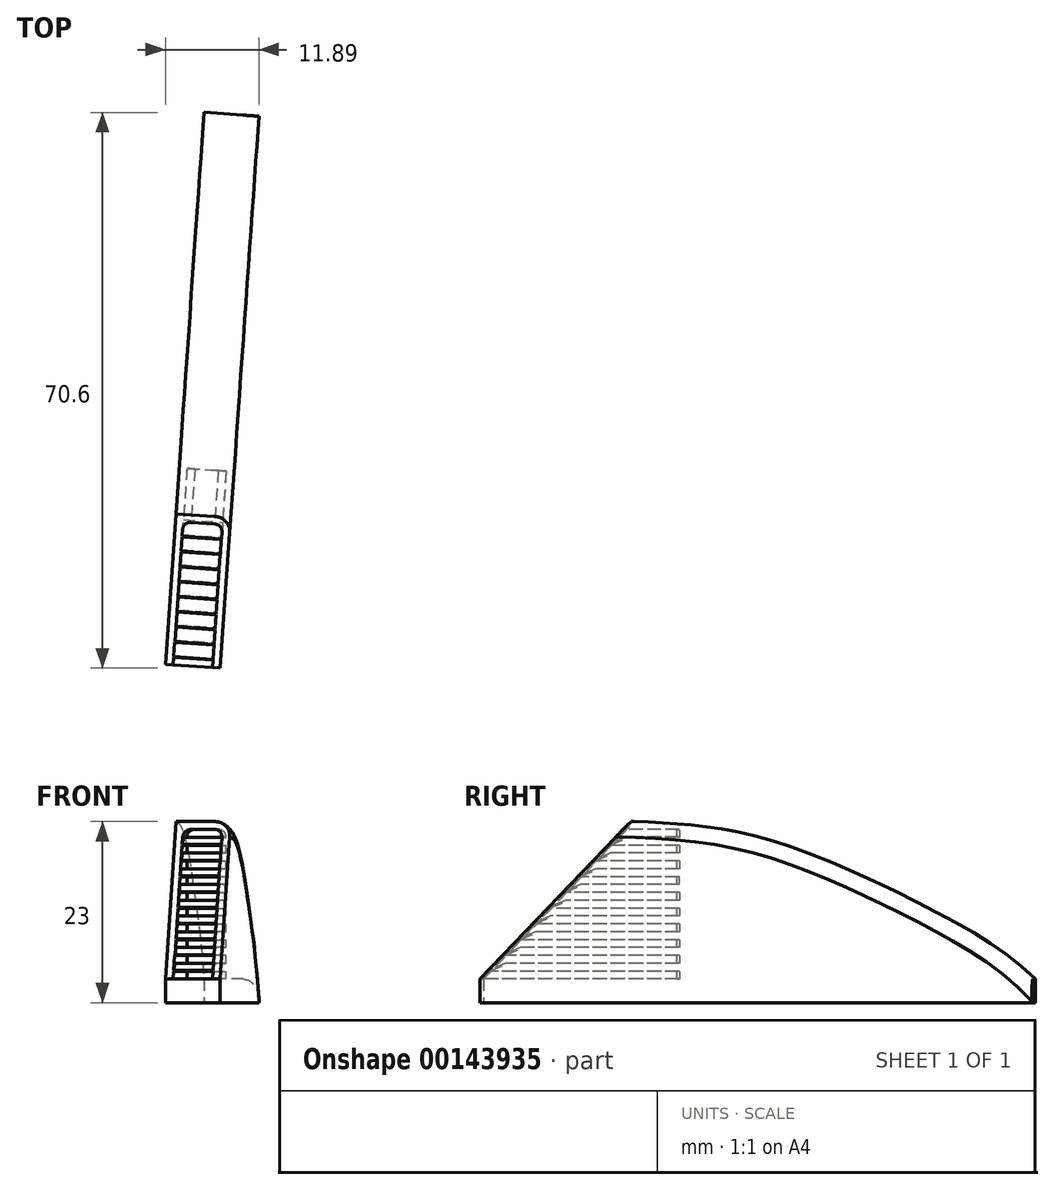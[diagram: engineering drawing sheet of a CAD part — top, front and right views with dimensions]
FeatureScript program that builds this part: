
annotation { "Feature Type Name" : "Feature", "Feature Type Description" : "" }
export const myFeature = defineFeature(function(context is Context, id is Id, definition is map)
    precondition{}
    {
        {
            var Q0;
            Q0=qCreatedBy(makeId("Top.planeOp"),FACE);
            var sketch = newSketch(context, id + "F0", { "sketchPlane" : qUnion([Q0])});
            skLineSegment(sketch, "E0", {"start": v(-28.15, -11.86) * mm, "end": v(-23.23, 58.25) * mm});
            skLineSegment(sketch, "E1", {"start": v(-30.2, 58.74) * mm, "end": v(-35.12, -11.37) * mm});
            skLineSegment(sketch, "E2", {"start": v(-23.23, 58.25) * mm, "end": v(-30.2, 58.74) * mm});
            skLineSegment(sketch, "E3", {"start": v(-28.15, -11.86) * mm, "end": v(-35.12, -11.37) * mm});
            skSolve(sketch);
        }
        {
            var Q0;
            Q0 = qSketchRegion(id + "F0", true);
            extrude(context, id + "F1", {"entities" : qUnion([Q0]), "depth" : 3 * mm});
        }
        {
            var Q0;
            Q0=makeQuery(id+"F1.opExtrude","CAP_FACE",FACE,{"disambiguationData":[OSD([sQuery(id+"F0.wireOp",EDGE,"mfbUUH89-GhNW-xkRt-vmny-iapurk2HKPIS"),sQuery(id+"F0.wireOp",EDGE,"E0"),sQuery(id+"F0.wireOp",EDGE,"JSxFqMj3-m5DG-nVDL-T3pK-i0W8c60JwMJz"),sQuery(id+"F0.wireOp",EDGE,"E1"),sQuery(id+"F0.wireOp",EDGE,"E2"),sQuery(id+"F0.wireOp",EDGE,"Zva8UKAF-Idc9-vliP-45KG-4Emh3L01odaY")])],"isStart":false});
            var sketch = newSketch(context, id + "F2", { "sketchPlane" : qUnion([Q0])});
            skLineSegment(sketch, "E4", {"start": v(-30.2, 58.74) * mm, "end": v(-30.2, 58.74) * mm});
            skLineSegment(sketch, "E5", {"start": v(-30.2, 58.74) * mm, "end": v(-35.12, -11.37) * mm});
            skLineSegment(sketch, "E6", {"start": v(-35.12, -11.37) * mm, "end": v(-28.15, -11.86) * mm});
            skLineSegment(sketch, "E7", {"start": v(-30.2, 58.74) * mm, "end": v(-23.23, 58.25) * mm});
            skLineSegment(sketch, "E8", {"start": v(-23.23, 58.25) * mm, "end": v(-28.15, -11.86) * mm});
            skSolve(sketch);
        }
        {
            var Q0;
            Q0 = qSketchRegion(id + "F2", true);
            extrude(context, id + "F3", {"entities" : qUnion([Q0]), "operationType" : NewBodyOperationType.ADD, "depth" : 20 * mm});
        }
        {
            var Q0;
            Q0=makeQuery(id+"F3.boolean.opBoolean","MERGE",FACE,{"derivedFrom":[makeQuery(id+"F1.opExtrude","SWEPT_FACE",FACE,{"disambiguationData":[OSD([sQuery(id+"F0.wireOp",EDGE,"E1")])]}),makeQuery(id+"F3.opExtrude","SWEPT_FACE",FACE,{"disambiguationData":[OSD([sQuery(id+"F2.wireOp",EDGE,"E5")])]})]});
            var sketch = newSketch(context, id + "F4", { "sketchPlane" : qUnion([Q0])});
            skLineSegment(sketch, "E9", {"start": v(13.8, 3) * mm, "end": v(-5.36, 23) * mm});
            skFitSpline(sketch, "E10", {"points": [v(-5.36, 23) * mm, v(-13.54, 22.46) * mm, v(-24.86, 19.96) * mm, v(-43.34, 11.76) * mm, v(-56.48, 3) * mm], "startDerivative": vector(-41.6, -1.3) * mm, "endDerivative": vector(-39.84, -39.3) * mm});
            skLineSegment(sketch, "E11", {"start": v(-56.48, 3) * mm, "end": v(-61.7, 3) * mm});
            skLineSegment(sketch, "E12", {"start": v(-61.7, 3) * mm, "end": v(-61.7, 25.73) * mm});
            skLineSegment(sketch, "E13", {"start": v(-61.7, 25.73) * mm, "end": v(18.56, 25.73) * mm});
            skLineSegment(sketch, "E14", {"start": v(18.56, 25.73) * mm, "end": v(13.8, 3) * mm});
            skSolve(sketch);
        }
        {
            var Q0;
            Q0 = qSketchRegion(id + "F4", true);
            extrude(context, id + "F5", {"entities" : qUnion([Q0]), "operationType" : NewBodyOperationType.REMOVE, "oppositeDirection" : true, "depth" : 25 * mm});
        }
        {
            var Q0;
            Q0=makeQuery(id+"F5.boolean.opBoolean","COPY",EDGE,{"derivedFrom":makeQuery(id+"F5.opExtrude","CAP_EDGE",EDGE,{"disambiguationData":[OSD([sQuery(id+"F4.wireOp",EDGE,"E10")])],"isStart":true})});
            var Q1;
            Q1=makeQuery(id+"F5.boolean.opBoolean","INTERSECT",EDGE,{"derivedFrom":[makeQuery(id+"F3.boolean.opBoolean","MERGE",FACE,{"derivedFrom":[makeQuery(id+"F1.opExtrude","SWEPT_FACE",FACE,{"disambiguationData":[OSD([sQuery(id+"F0.wireOp",EDGE,"E0")])]}),makeQuery(id+"F3.opExtrude","SWEPT_FACE",FACE,{"disambiguationData":[OSD([sQuery(id+"F2.wireOp",EDGE,"E8")])]})]}),makeQuery(id+"F5.opExtrude","SWEPT_FACE",FACE,{"disambiguationData":[OSD([sQuery(id+"F4.wireOp",EDGE,"E10")])]})]});
            fillet(context, id + "F6", {"entities" : qUnion([Q0, Q1]), "radius" : 2 * mm, "tangentPropagation" : true, "allowEdgeOverflow" : false});
        }
        {
            var Q0;
            Q0=makeQuery(id+"F3.boolean.opBoolean","MERGE",FACE,{"derivedFrom":[makeQuery(id+"F1.opExtrude","SWEPT_FACE",FACE,{"disambiguationData":[OSD([sQuery(id+"F0.wireOp",EDGE,"E3")])]}),makeQuery(id+"F3.opExtrude","SWEPT_FACE",FACE,{"disambiguationData":[OSD([sQuery(id+"F2.wireOp",EDGE,"E6")])]})]});
            var sketch = newSketch(context, id + "F7", { "sketchPlane" : qUnion([Q0])});
            skLineSegment(sketch, "E15.0", {"start": v(-33.23, 4) * mm, "end": v(-28.25, 4) * mm});
            skFitSpline(sketch, "E15.1", {"points": [v(-28.25, 21.06) * mm, v(-28.25, 21.11) * mm, v(-28.26, 21.21) * mm, v(-28.3, 21.37) * mm, v(-28.38, 21.52) * mm, v(-28.48, 21.66) * mm, v(-28.62, 21.8) * mm, v(-28.86, 21.94) * mm, v(-29.1, 22) * mm, v(-29.25, 22) * mm]});
            skLineSegment(sketch, "E15.2", {"start": v(-29.25, 22) * mm, "end": v(-32.23, 22) * mm});
            skLineSegment(sketch, "E15.3", {"start": v(-28.25, 5) * mm, "end": v(-28.25, 6) * mm});
            skFitSpline(sketch, "E15.4", {"points": [v(-32.23, 22) * mm, v(-32.32, 22) * mm, v(-32.43, 21.99) * mm, v(-32.58, 21.94) * mm, v(-32.72, 21.89) * mm, v(-32.87, 21.8) * mm, v(-33.05, 21.62) * mm, v(-33.2, 21.37) * mm, v(-33.23, 21.16) * mm, v(-33.23, 21.06) * mm]});
            skLineSegment(sketch, "E15.5", {"start": v(-33.23, 21.06) * mm, "end": v(-33.23, 21) * mm});
            skLineSegment(sketch, "E16.0", {"start": v(-33.23, 5) * mm, "end": v(-28.25, 5) * mm});
            skLineSegment(sketch, "E17.0.1.0", {"start": v(-33.23, 6) * mm, "end": v(-28.25, 6) * mm});
            skLineSegment(sketch, "E17.0.2.0", {"start": v(-33.23, 7) * mm, "end": v(-28.25, 7) * mm});
            skLineSegment(sketch, "E17.0.3.0", {"start": v(-33.23, 8) * mm, "end": v(-28.25, 8) * mm});
            skLineSegment(sketch, "E17.0.4.0", {"start": v(-33.23, 9) * mm, "end": v(-28.25, 9) * mm});
            skLineSegment(sketch, "E17.0.5.0", {"start": v(-33.23, 10) * mm, "end": v(-28.25, 10) * mm});
            skLineSegment(sketch, "E17.0.6.0", {"start": v(-33.23, 11) * mm, "end": v(-28.25, 11) * mm});
            skLineSegment(sketch, "E17.0.7.0", {"start": v(-33.23, 12) * mm, "end": v(-28.25, 12) * mm});
            skLineSegment(sketch, "E17.0.8.0", {"start": v(-33.23, 13) * mm, "end": v(-28.25, 13) * mm});
            skLineSegment(sketch, "E17.0.9.0", {"start": v(-33.23, 14) * mm, "end": v(-28.25, 14) * mm});
            skLineSegment(sketch, "E17.0.10.0", {"start": v(-33.23, 15) * mm, "end": v(-28.25, 15) * mm});
            skLineSegment(sketch, "E17.0.11.0", {"start": v(-33.23, 16) * mm, "end": v(-28.25, 16) * mm});
            skLineSegment(sketch, "E17.0.12.0", {"start": v(-33.23, 17) * mm, "end": v(-28.25, 17) * mm});
            skLineSegment(sketch, "E17.0.13.0", {"start": v(-33.23, 18) * mm, "end": v(-28.25, 18) * mm});
            skLineSegment(sketch, "E17.0.14.0", {"start": v(-33.23, 19) * mm, "end": v(-28.25, 19) * mm});
            skLineSegment(sketch, "E17.0.15.0", {"start": v(-33.23, 20) * mm, "end": v(-28.25, 20) * mm});
            skLineSegment(sketch, "E17.0.16.0", {"start": v(-33.23, 21) * mm, "end": v(-28.25, 21) * mm});
            skLineSegment(sketch, "E17.direction2", {"start": v(-33.23, 5) * mm, "end": v(-33.23, 6) * mm, "construction": true});
            skLineSegment(sketch, "E18.trimOffspring", {"start": v(-33.23, 20) * mm, "end": v(-33.23, 19) * mm});
            skLineSegment(sketch, "E19.trimOffspring", {"start": v(-28.25, 21) * mm, "end": v(-28.25, 21.06) * mm});
            skLineSegment(sketch, "E20.trimOffspring", {"start": v(-28.25, 19) * mm, "end": v(-28.25, 20) * mm});
            skLineSegment(sketch, "E21.trimOffspring", {"start": v(-33.23, 18) * mm, "end": v(-33.23, 17) * mm});
            skLineSegment(sketch, "E22.trimOffspring", {"start": v(-28.25, 17) * mm, "end": v(-28.25, 18) * mm});
            skLineSegment(sketch, "E23.trimOffspring", {"start": v(-28.25, 15) * mm, "end": v(-28.25, 16) * mm});
            skLineSegment(sketch, "E24.trimOffspring", {"start": v(-33.23, 14) * mm, "end": v(-33.23, 13) * mm});
            skLineSegment(sketch, "E25.trimOffspring", {"start": v(-28.25, 13) * mm, "end": v(-28.25, 14) * mm});
            skLineSegment(sketch, "E26.trimOffspring", {"start": v(-33.23, 12) * mm, "end": v(-33.23, 11) * mm});
            skLineSegment(sketch, "E27", {"start": v(-33.23, 15) * mm, "end": v(-33.23, 16) * mm});
            skLineSegment(sketch, "E28.trimOffspring", {"start": v(-28.25, 11) * mm, "end": v(-28.25, 12) * mm});
            skLineSegment(sketch, "E29.trimOffspring", {"start": v(-33.23, 10) * mm, "end": v(-33.23, 9) * mm});
            skLineSegment(sketch, "E30.trimOffspring", {"start": v(-28.25, 9) * mm, "end": v(-28.25, 10) * mm});
            skLineSegment(sketch, "E31.trimOffspring", {"start": v(-33.23, 8) * mm, "end": v(-33.23, 7) * mm});
            skLineSegment(sketch, "E32.trimOffspring", {"start": v(-28.25, 7) * mm, "end": v(-28.25, 8) * mm});
            skLineSegment(sketch, "E33.trimOffspring", {"start": v(-33.23, 6) * mm, "end": v(-33.23, 5) * mm});
            skLineSegment(sketch, "E34", {"start": v(-33.23, 4) * mm, "end": v(-33.23, 3) * mm});
            skLineSegment(sketch, "E35", {"start": v(-33.23, 3) * mm, "end": v(-28.25, 3) * mm});
            skLineSegment(sketch, "E36", {"start": v(-28.25, 3) * mm, "end": v(-28.25, 4) * mm});
            skSolve(sketch);
        }
        {
            var Q0;
            Q0 = qSketchRegion(id + "F7", true);
            extrude(context, id + "F8", {"entities" : qUnion([Q0]), "operationType" : NewBodyOperationType.REMOVE, "oppositeDirection" : true, "depth" : 25 * mm});
        }
        {
            var Q0;
            Q0=makeQuery(id+"F8.boolean.opBoolean","INTERSECT",EDGE,{"derivedFrom":[makeQuery(id+"F5.boolean.opBoolean","COPY",FACE,{"derivedFrom":makeQuery(id+"F5.opExtrude","SWEPT_FACE",FACE,{"disambiguationData":[OSD([sQuery(id+"F4.wireOp",EDGE,"E9")])]})}),makeQuery(id+"F8.opExtrude","SWEPT_FACE",FACE,{"disambiguationData":[OSD([sQuery(id+"F7.wireOp",EDGE,"E17.0.16.0")])]})]});
            var Q1;
            Q1=makeQuery(id+"F8.boolean.opBoolean","INTERSECT",EDGE,{"derivedFrom":[makeQuery(id+"F5.boolean.opBoolean","COPY",FACE,{"derivedFrom":makeQuery(id+"F5.opExtrude","SWEPT_FACE",FACE,{"disambiguationData":[OSD([sQuery(id+"F4.wireOp",EDGE,"E9")])]})}),makeQuery(id+"F8.opExtrude","SWEPT_FACE",FACE,{"disambiguationData":[OSD([sQuery(id+"F7.wireOp",EDGE,"E17.0.14.0")])]})]});
            var Q2;
            Q2=makeQuery(id+"F8.boolean.opBoolean","INTERSECT",EDGE,{"derivedFrom":[makeQuery(id+"F5.boolean.opBoolean","COPY",FACE,{"derivedFrom":makeQuery(id+"F5.opExtrude","SWEPT_FACE",FACE,{"disambiguationData":[OSD([sQuery(id+"F4.wireOp",EDGE,"E9")])]})}),makeQuery(id+"F8.opExtrude","SWEPT_FACE",FACE,{"disambiguationData":[OSD([sQuery(id+"F7.wireOp",EDGE,"E17.0.12.0")])]})]});
            var Q3;
            Q3=makeQuery(id+"F8.boolean.opBoolean","INTERSECT",EDGE,{"derivedFrom":[makeQuery(id+"F5.boolean.opBoolean","COPY",FACE,{"derivedFrom":makeQuery(id+"F5.opExtrude","SWEPT_FACE",FACE,{"disambiguationData":[OSD([sQuery(id+"F4.wireOp",EDGE,"E9")])]})}),makeQuery(id+"F8.opExtrude","SWEPT_FACE",FACE,{"disambiguationData":[OSD([sQuery(id+"F7.wireOp",EDGE,"E17.0.10.0")])]})]});
            var Q4;
            Q4=makeQuery(id+"F8.boolean.opBoolean","INTERSECT",EDGE,{"derivedFrom":[makeQuery(id+"F5.boolean.opBoolean","COPY",FACE,{"derivedFrom":makeQuery(id+"F5.opExtrude","SWEPT_FACE",FACE,{"disambiguationData":[OSD([sQuery(id+"F4.wireOp",EDGE,"E9")])]})}),makeQuery(id+"F8.opExtrude","SWEPT_FACE",FACE,{"disambiguationData":[OSD([sQuery(id+"F7.wireOp",EDGE,"E17.0.8.0")])]})]});
            var Q5;
            Q5=makeQuery(id+"F8.boolean.opBoolean","INTERSECT",EDGE,{"derivedFrom":[makeQuery(id+"F5.boolean.opBoolean","COPY",FACE,{"derivedFrom":makeQuery(id+"F5.opExtrude","SWEPT_FACE",FACE,{"disambiguationData":[OSD([sQuery(id+"F4.wireOp",EDGE,"E9")])]})}),makeQuery(id+"F8.opExtrude","SWEPT_FACE",FACE,{"disambiguationData":[OSD([sQuery(id+"F7.wireOp",EDGE,"E17.0.6.0")])]})]});
            var Q6;
            Q6=makeQuery(id+"F8.boolean.opBoolean","INTERSECT",EDGE,{"derivedFrom":[makeQuery(id+"F5.boolean.opBoolean","COPY",FACE,{"derivedFrom":makeQuery(id+"F5.opExtrude","SWEPT_FACE",FACE,{"disambiguationData":[OSD([sQuery(id+"F4.wireOp",EDGE,"E9")])]})}),makeQuery(id+"F8.opExtrude","SWEPT_FACE",FACE,{"disambiguationData":[OSD([sQuery(id+"F7.wireOp",EDGE,"E17.0.4.0")])]})]});
            var Q7;
            Q7=makeQuery(id+"F8.boolean.opBoolean","INTERSECT",EDGE,{"derivedFrom":[makeQuery(id+"F5.boolean.opBoolean","COPY",FACE,{"derivedFrom":makeQuery(id+"F5.opExtrude","SWEPT_FACE",FACE,{"disambiguationData":[OSD([sQuery(id+"F4.wireOp",EDGE,"E9")])]})}),makeQuery(id+"F8.opExtrude","SWEPT_FACE",FACE,{"disambiguationData":[OSD([sQuery(id+"F7.wireOp",EDGE,"E17.0.2.0")])]})]});
            var Q8;
            Q8=makeQuery(id+"F8.boolean.opBoolean","INTERSECT",EDGE,{"derivedFrom":[makeQuery(id+"F5.boolean.opBoolean","COPY",FACE,{"derivedFrom":makeQuery(id+"F5.opExtrude","SWEPT_FACE",FACE,{"disambiguationData":[OSD([sQuery(id+"F4.wireOp",EDGE,"E9")])]})}),makeQuery(id+"F8.opExtrude","SWEPT_FACE",FACE,{"disambiguationData":[OSD([sQuery(id+"F7.wireOp",EDGE,"E16.0")])]})]});
            chamfer(context, id + "F9", {"entities" : qUnion([Q0, Q1, Q2, Q3, Q4, Q5, Q6, Q7, Q8]), "width" : 1.25 * mm, "tangentPropagation" : true});
        }
    });
